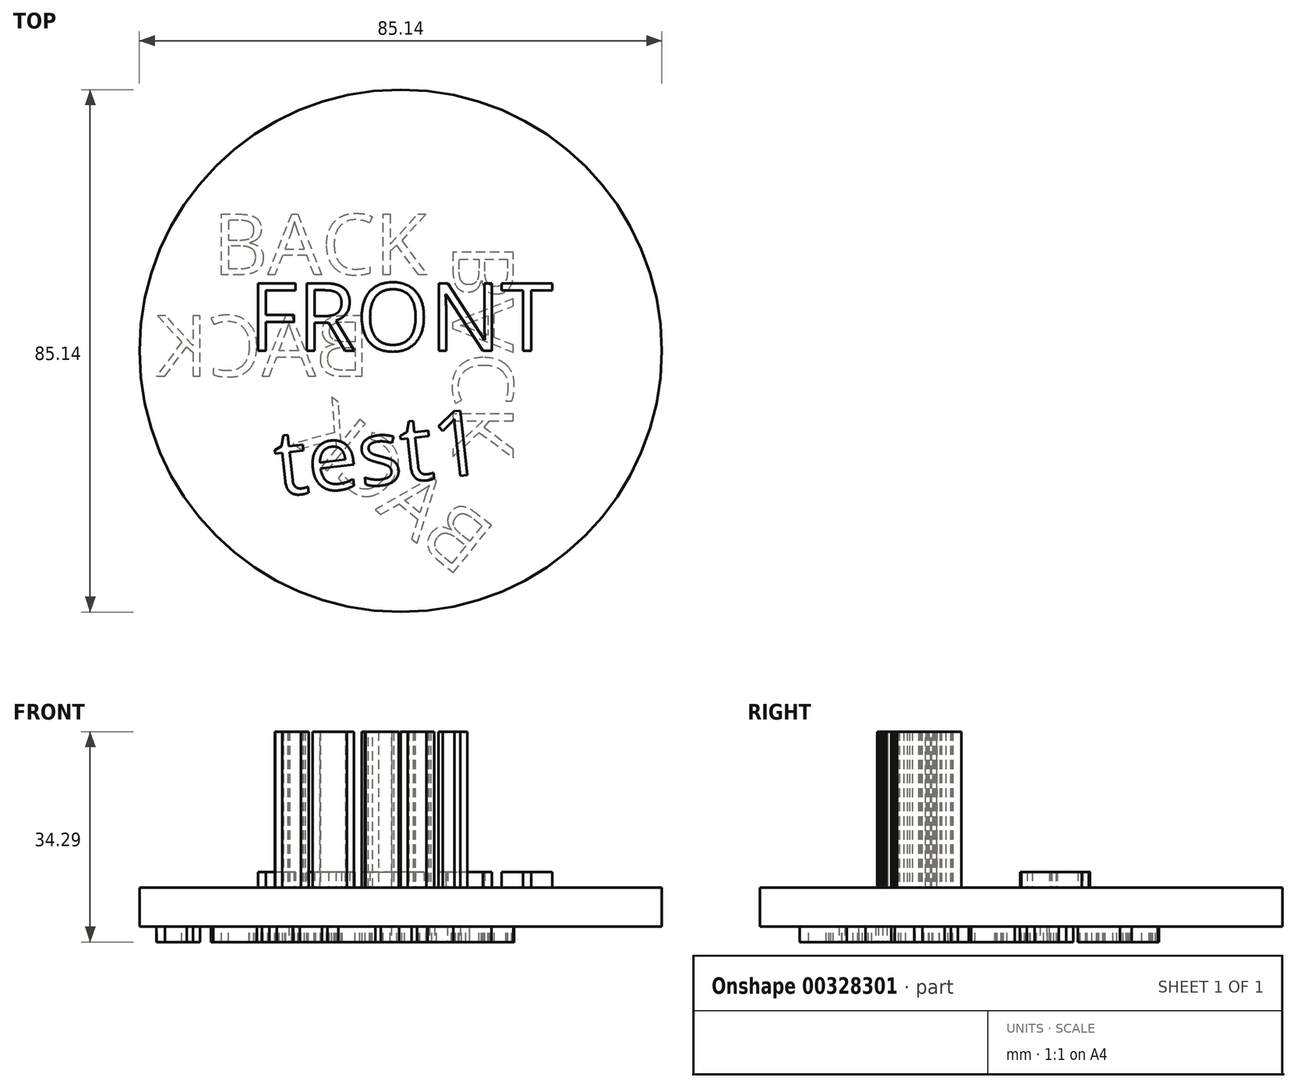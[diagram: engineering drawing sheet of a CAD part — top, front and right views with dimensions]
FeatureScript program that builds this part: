
annotation { "Feature Type Name" : "Feature", "Feature Type Description" : "" }
export const myFeature = defineFeature(function(context is Context, id is Id, definition is map)
    precondition{}
    {
        {
            var Q0;
            Q0=qCreatedBy(makeId("Top.planeOp"),FACE);
            var sketch = newSketch(context, id + "F0", { "sketchPlane" : qUnion([Q0])});
            skCircle(sketch, "E0", {"center": v(0, 0) * mm, "radius": 42.57 * mm});
            skSolve(sketch);
        }
        {
            var Q0;
            Q0=makeQuery(id+"F0.imprint","IMPRINT",FACE,{"disambiguationData":[TD([[makeQuery(id+"F0.imprint","IMPRINT",EDGE,{"derivedFrom":sQuery(id+"F0.wireOp",EDGE,"E0")}),1.0]])]});
            extrude(context, id + "F1", {"entities" : qUnion([Q0]), "depth" : 6.35 * mm});
        }
        {
            var Q0;
            Q0=makeQuery(id+"F1.opExtrude","CAP_FACE",FACE,{"disambiguationData":[OSD([sQuery(id+"F0.wireOp",EDGE,"E0")])],"isStart":false});
            var sketch = newSketch(context, id + "F2", { "sketchPlane" : qUnion([Q0])});
            skText(sketch, "E1", { "text": "FRONT", "fontName": "OpenSans-Regular.ttf"});
            const initialGuessF2  = {"E1": [-0.02476, 0, 1, 0, 0.0111]};
            skSetInitialGuess(sketch, initialGuessF2);
            skSolve(sketch);
        }
        {
            var Q0;
            Q0=qSketchRegion(id+"F2",true);
            extrude(context, id + "F3", {"entities" : qUnion([Q0]), "operationType" : NewBodyOperationType.ADD, "depth" : 2.54 * mm});
        }
        {
            var Q0;
            Q0=makeQuery(id+"F1.opExtrude","CAP_FACE",FACE,{"disambiguationData":[OSD([sQuery(id+"F0.wireOp",EDGE,"E0")])],"isStart":true});
            var sketch = newSketch(context, id + "F4", { "sketchPlane" : qUnion([Q0])});
            skText(sketch, "E2", { "text": "BACK", "fontName": "OpenSans-Regular.ttf"});
            skText(sketch, "E3", { "text": "BACK", "fontName": "OpenSans-Regular.ttf"});
            skText(sketch, "E4", { "text": "BACK", "fontName": "OpenSans-Regular.ttf"});
            const initialGuessF4  = {"E2": [-0.00492, 0.00414, -1, 0, 0.00994], "E3": [0.01838, -0.01744, 0, 1, 0.00994], "E4": [0.00965, 0.03698, -0.77875, -0.62733, 0.00994]};
            skSetInitialGuess(sketch, initialGuessF4);
            skSolve(sketch);
        }
        {
            var Q0;
            Q0=qSketchRegion(id+"F4",true);
            extrude(context, id + "F5", {"entities" : qUnion([Q0]), "operationType" : NewBodyOperationType.ADD, "depth" : 2.54 * mm});
        }
        {
            var Q0;
            {var subQ0=sQuery(id+"F0.wireOp",EDGE,"E0");Q0=makeQuery(id+"F3.boolean.opBoolean","SPLIT",FACE,{"disambiguationData":[TD([makeQuery(id+"F1.opExtrude","SWEPT_FACE",FACE,{"disambiguationData":[OSD([subQ0])]})])],"derivedFrom":makeQuery(id+"F1.opExtrude","CAP_FACE",FACE,{"disambiguationData":[OSD([subQ0])],"isStart":false})});}
            var sketch = newSketch(context, id + "F6", { "sketchPlane" : qUnion([Q0])});
            skText(sketch, "E5", { "text": "BACK\n", "fontName": "OpenSans-Regular.ttf"});
            const initialGuessF6  = {"E5": [-0.03058, 0.01242, 1, 0, 0.00994]};
            skSetInitialGuess(sketch, initialGuessF6);
            skSolve(sketch);
        }
        {
            var Q0;
            Q0=qSketchRegion(id+"F6",true);
            var Q1;
            Q1=makeQuery(id+"F5.opExtrude","CAP_FACE",FACE,{"disambiguationData":[OSD([sQuery(id+"F4.wireOp",EDGE,"E2.sketch_text.stroke-0"),sQuery(id+"F4.wireOp",EDGE,"E2.sketch_text.stroke-1"),sQuery(id+"F4.wireOp",EDGE,"E2.sketch_text.stroke-2"),sQuery(id+"F4.wireOp",EDGE,"E2.sketch_text.stroke-3"),sQuery(id+"F4.wireOp",EDGE,"E2.sketch_text.stroke-4"),sQuery(id+"F4.wireOp",EDGE,"E2.sketch_text.stroke-5"),sQuery(id+"F4.wireOp",EDGE,"E2.sketch_text.stroke-6"),sQuery(id+"F4.wireOp",EDGE,"E2.sketch_text.stroke-7"),sQuery(id+"F4.wireOp",EDGE,"E2.sketch_text.stroke-8"),sQuery(id+"F4.wireOp",EDGE,"E2.sketch_text.stroke-9"),sQuery(id+"F4.wireOp",EDGE,"E2.sketch_text.stroke-10"),sQuery(id+"F4.wireOp",EDGE,"E2.sketch_text.stroke-11"),sQuery(id+"F4.wireOp",EDGE,"E2.sketch_text.stroke-12"),sQuery(id+"F4.wireOp",EDGE,"E2.sketch_text.stroke-13"),sQuery(id+"F4.wireOp",EDGE,"E2.sketch_text.stroke-14"),sQuery(id+"F4.wireOp",EDGE,"E2.sketch_text.stroke-15"),sQuery(id+"F4.wireOp",EDGE,"E2.sketch_text.stroke-16"),sQuery(id+"F4.wireOp",EDGE,"E2.sketch_text.stroke-17"),sQuery(id+"F4.wireOp",EDGE,"E2.sketch_text.stroke-18"),sQuery(id+"F4.wireOp",EDGE,"E2.sketch_text.stroke-19"),sQuery(id+"F4.wireOp",EDGE,"E2.sketch_text.stroke-20"),sQuery(id+"F4.wireOp",EDGE,"E2.sketch_text.stroke-21"),sQuery(id+"F4.wireOp",EDGE,"E2.sketch_text.stroke-22"),sQuery(id+"F4.wireOp",EDGE,"E2.sketch_text.stroke-23"),sQuery(id+"F4.wireOp",EDGE,"E2.sketch_text.stroke-24")])],"isStart":false});
            extrude(context, id + "F7", {"entities" : qUnion([Q0]), "operationType" : NewBodyOperationType.ADD, "endBound" : BoundingType.UP_TO_SURFACE, "oppositeDirection" : true, "endBoundEntityFace" : qUnion([Q1]), "depth" : 25.4 * mm});
        }
        {
            var Q0;
            {var subQ0=sQuery(id+"F0.wireOp",EDGE,"E0");Q0=makeQuery(id+"F3.boolean.opBoolean","SPLIT",FACE,{"disambiguationData":[TD([makeQuery(id+"F1.opExtrude","SWEPT_FACE",FACE,{"disambiguationData":[OSD([subQ0])]})])],"derivedFrom":makeQuery(id+"F1.opExtrude","CAP_FACE",FACE,{"disambiguationData":[OSD([subQ0])],"isStart":false})});}
            var sketch = newSketch(context, id + "F8", { "sketchPlane" : qUnion([Q0])});
            skText(sketch, "E6", { "text": "test1", "fontName": "OpenSans-Regular.ttf"});
            skLineSegment(sketch, "E7", {"start": v(-21.66, -7.66) * mm, "end": v(-0.95, -5.33) * mm, "construction": true});
            const initialGuessF8  = {"E6": [-0.01988, -0.0237, 0.99374, 0.11172, 0.01065]};
            skSetInitialGuess(sketch, initialGuessF8);
            skSolve(sketch);
        }
        {
            var Q0;
            Q0 = qSketchRegion(id + "F8", true);
            extrude(context, id + "F9", {"entities" : qUnion([Q0]), "operationType" : NewBodyOperationType.ADD, "depth" : 25.4 * mm});
        }
    });
